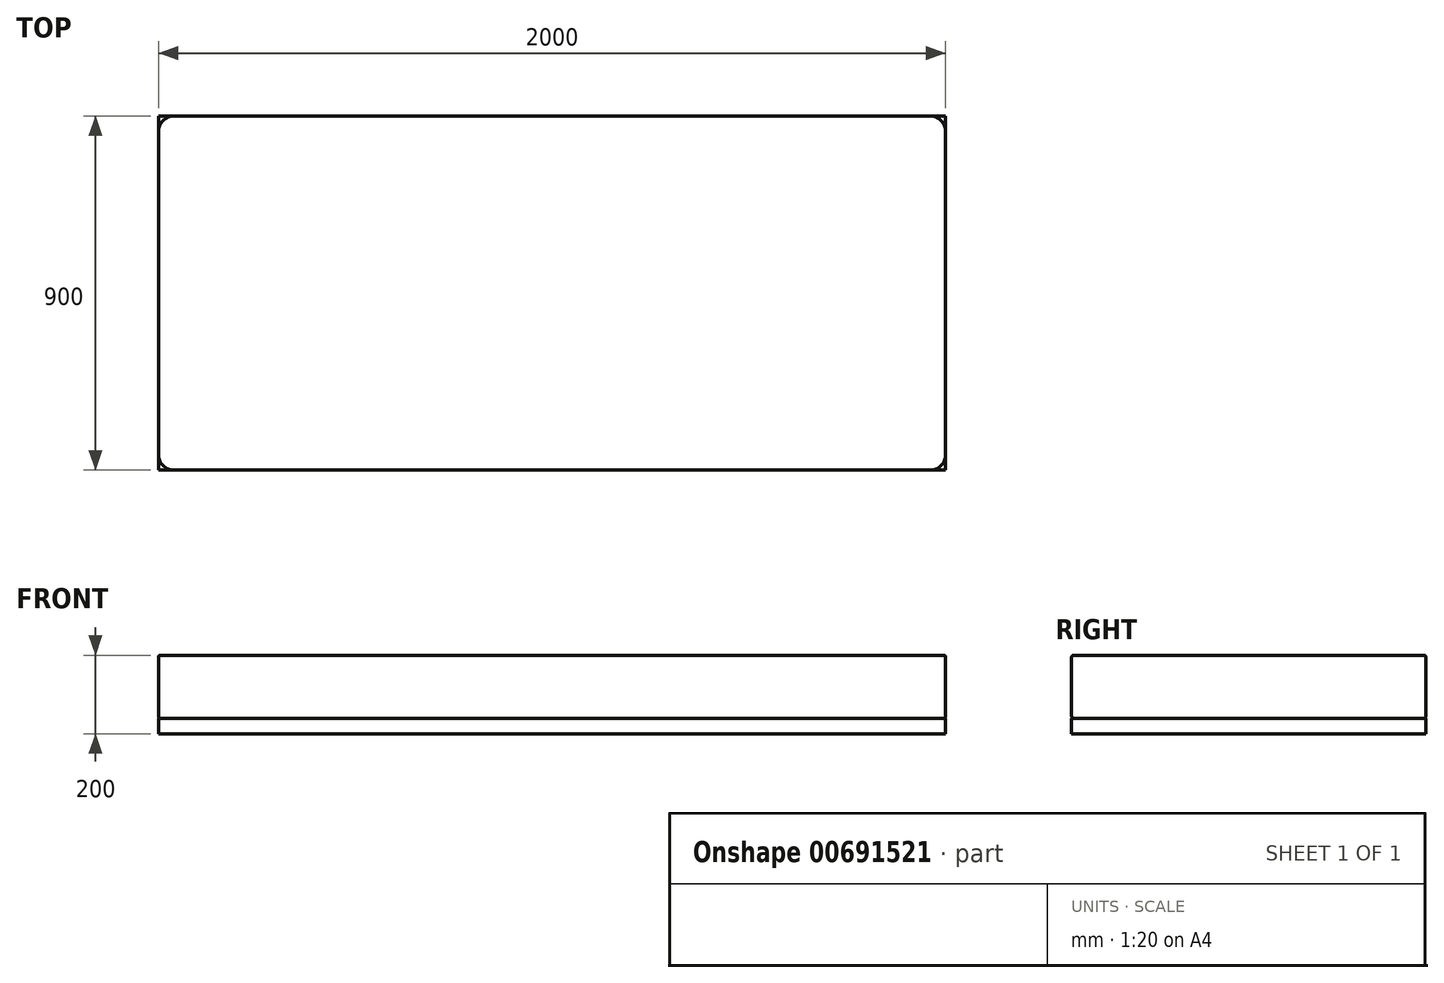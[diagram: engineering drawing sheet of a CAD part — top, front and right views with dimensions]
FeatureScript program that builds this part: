
annotation { "Feature Type Name" : "Feature", "Feature Type Description" : "" }
export const myFeature = defineFeature(function(context is Context, id is Id, definition is map)
    precondition{}
    {
        {
            var Q0;
            Q0=qCreatedBy(makeId("Top.planeOp"),FACE);
            var sketch = newSketch(context, id + "F0", { "sketchPlane" : qUnion([Q0])});
            skLineSegment(sketch, "E0.bottom", {"start": v(0, 0) * mm, "end": v(2000, 0) * mm});
            skLineSegment(sketch, "E0.top", {"start": v(0, -900) * mm, "end": v(2000, -900) * mm});
            skLineSegment(sketch, "E0.left", {"start": v(0, 0) * mm, "end": v(0, -900) * mm});
            skLineSegment(sketch, "E0.right", {"start": v(2000, 0) * mm, "end": v(2000, -900) * mm});
            skSolve(sketch);
        }
        {
            var Q0;
            Q0=makeQuery(id+"F0.imprint","IMPRINT",FACE,{"disambiguationData":[TD([[makeQuery(id+"F0.imprint","IMPRINT",EDGE,{"derivedFrom":sQuery(id+"F0.wireOp",EDGE,"E0.bottom")}),-1.0]])]});
            extrude(context, id + "F1", {"entities" : qUnion([Q0]), "depth" : 40 * mm, "offsetDistance" : 25 * mm});
        }
        {
            var Q0;
            Q0=makeQuery(id+"F1.opExtrude","CAP_FACE",FACE,{"disambiguationData":[OSD([sQuery(id+"F0.wireOp",EDGE,"E0.bottom"),sQuery(id+"F0.wireOp",EDGE,"E0.top"),sQuery(id+"F0.wireOp",EDGE,"E0.left"),sQuery(id+"F0.wireOp",EDGE,"E0.right")])],"isStart":false});
            extrude(context, id + "F2", {"entities" : qUnion([Q0]), "depth" : 160 * mm, "offsetDistance" : 25 * mm});
        }
        {
            var Q0;
            Q0=makeQuery(id+"F2.opExtrude","SWEPT_EDGE",EDGE,{"disambiguationData":[OSD([sQuery(id+"F0.wireOp",EDGE,"E0.top"),sQuery(id+"F0.wireOp",EDGE,"E0.left")])]});
            var Q1;
            Q1=makeQuery(id+"F2.opExtrude","SWEPT_EDGE",EDGE,{"disambiguationData":[OSD([sQuery(id+"F0.wireOp",EDGE,"E0.bottom"),sQuery(id+"F0.wireOp",EDGE,"E0.left")])]});
            var Q2;
            Q2=makeQuery(id+"F2.opExtrude","SWEPT_EDGE",EDGE,{"disambiguationData":[OSD([sQuery(id+"F0.wireOp",EDGE,"E0.top"),sQuery(id+"F0.wireOp",EDGE,"E0.right")])]});
            var Q3;
            Q3=makeQuery(id+"F2.opExtrude","SWEPT_EDGE",EDGE,{"disambiguationData":[OSD([sQuery(id+"F0.wireOp",EDGE,"E0.bottom"),sQuery(id+"F0.wireOp",EDGE,"E0.right")])]});
            fillet(context, id + "F3", {"entities" : qUnion([Q0, Q1, Q2, Q3]), "radius" : 40 * mm, "tangentPropagation" : true, "allowEdgeOverflow" : false});
        }
        {
            var Q0;
            Q0=makeQuery(id+"F2.opExtrude","CAP_EDGE",EDGE,{"disambiguationData":[OSD([sQuery(id+"F0.wireOp",EDGE,"E0.right")])],"isStart":false});
            var Q1;
            Q1=makeQuery(id+"F2.opExtrude","CAP_EDGE",EDGE,{"disambiguationData":[OSD([sQuery(id+"F0.wireOp",EDGE,"E0.left")])],"isStart":false});
            var Q2;
            Q2=makeQuery(id+"F2.opExtrude","CAP_EDGE",EDGE,{"disambiguationData":[OSD([sQuery(id+"F0.wireOp",EDGE,"E0.bottom")])],"isStart":true});
            var Q3;
            Q3=makeQuery(id+"F2.opExtrude","CAP_EDGE",EDGE,{"disambiguationData":[OSD([sQuery(id+"F0.wireOp",EDGE,"E0.bottom")])],"isStart":false});
            var Q4;
            Q4=makeQuery(id+"F2.opExtrude","CAP_EDGE",EDGE,{"disambiguationData":[OSD([sQuery(id+"F0.wireOp",EDGE,"E0.top")])],"isStart":false});
            var Q5;
            {var subQ0=sQuery(id+"F0.wireOp",EDGE,"E0.right");var subQ1=sQuery(id+"F0.wireOp",EDGE,"E0.bottom");Q5=makeQuery(id+"F3.opFillet","BLEND_EDGE",EDGE,{"blendedFrom":[makeQuery(id+"F2.opExtrude","SWEPT_EDGE",EDGE,{"disambiguationData":[OSD([subQ1,subQ0])]}),makeQuery(id+"F2.opExtrude","CAP_FACE",FACE,{"disambiguationData":[OSD([subQ1,sQuery(id+"F0.wireOp",EDGE,"E0.top"),sQuery(id+"F0.wireOp",EDGE,"E0.left"),subQ0])],"isStart":false})],"blendedInto":[makeQuery(id+"F2.opExtrude","CAP_FACE",FACE,{"disambiguationData":[OSD([subQ1,sQuery(id+"F0.wireOp",EDGE,"E0.top"),sQuery(id+"F0.wireOp",EDGE,"E0.left"),subQ0])],"isStart":false})]});}
            var Q6;
            {var subQ0=sQuery(id+"F0.wireOp",EDGE,"E0.top");Q6=makeQuery(id+"F3.opFillet","BLEND_EDGE",EDGE,{"blendedFrom":[makeQuery(id+"F2.opExtrude","SWEPT_EDGE",EDGE,{"disambiguationData":[OSD([subQ0,sQuery(id+"F0.wireOp",EDGE,"E0.left")])]}),makeQuery(id+"F2.opExtrude","SWEPT_FACE",FACE,{"disambiguationData":[OSD([subQ0])]})],"blendedInto":[makeQuery(id+"F2.opExtrude","SWEPT_FACE",FACE,{"disambiguationData":[OSD([subQ0])]})]});}
            var Q7;
            {var subQ0=sQuery(id+"F0.wireOp",EDGE,"E0.left");Q7=makeQuery(id+"F3.opFillet","BLEND_EDGE",EDGE,{"blendedFrom":[makeQuery(id+"F2.opExtrude","SWEPT_EDGE",EDGE,{"disambiguationData":[OSD([sQuery(id+"F0.wireOp",EDGE,"E0.top"),subQ0])]}),makeQuery(id+"F2.opExtrude","SWEPT_FACE",FACE,{"disambiguationData":[OSD([subQ0])]})],"blendedInto":[makeQuery(id+"F2.opExtrude","SWEPT_FACE",FACE,{"disambiguationData":[OSD([subQ0])]})]});}
            var Q8;
            Q8=makeQuery(id+"F2.opExtrude","CAP_EDGE",EDGE,{"disambiguationData":[OSD([sQuery(id+"F0.wireOp",EDGE,"E0.right")])],"isStart":true});
            var Q9;
            {var subQ0=sQuery(id+"F0.wireOp",EDGE,"E0.left");var subQ1=sQuery(id+"F0.wireOp",EDGE,"E0.bottom");Q9=makeQuery(id+"F3.opFillet","BLEND_EDGE",EDGE,{"blendedFrom":[makeQuery(id+"F2.opExtrude","SWEPT_EDGE",EDGE,{"disambiguationData":[OSD([subQ1,subQ0])]}),makeQuery(id+"F2.opExtrude","CAP_FACE",FACE,{"disambiguationData":[OSD([subQ1,sQuery(id+"F0.wireOp",EDGE,"E0.top"),subQ0,sQuery(id+"F0.wireOp",EDGE,"E0.right")])],"isStart":false})],"blendedInto":[makeQuery(id+"F2.opExtrude","CAP_FACE",FACE,{"disambiguationData":[OSD([subQ1,sQuery(id+"F0.wireOp",EDGE,"E0.top"),subQ0,sQuery(id+"F0.wireOp",EDGE,"E0.right")])],"isStart":false})]});}
            var Q10;
            Q10=makeQuery(id+"F2.opExtrude","CAP_EDGE",EDGE,{"disambiguationData":[OSD([sQuery(id+"F0.wireOp",EDGE,"E0.left")])],"isStart":true});
            var Q11;
            {var subQ0=sQuery(id+"F0.wireOp",EDGE,"E0.left");var subQ1=sQuery(id+"F0.wireOp",EDGE,"E0.top");Q11=makeQuery(id+"F3.opFillet","BLEND_EDGE",EDGE,{"blendedFrom":[makeQuery(id+"F2.opExtrude","SWEPT_EDGE",EDGE,{"disambiguationData":[OSD([subQ1,subQ0])]}),makeQuery(id+"F2.opExtrude","CAP_FACE",FACE,{"disambiguationData":[OSD([sQuery(id+"F0.wireOp",EDGE,"E0.bottom"),subQ1,subQ0,sQuery(id+"F0.wireOp",EDGE,"E0.right")])],"isStart":true})],"blendedInto":[makeQuery(id+"F2.opExtrude","CAP_FACE",FACE,{"disambiguationData":[OSD([sQuery(id+"F0.wireOp",EDGE,"E0.bottom"),subQ1,subQ0,sQuery(id+"F0.wireOp",EDGE,"E0.right")])],"isStart":true})]});}
            var Q12;
            {var subQ0=sQuery(id+"F0.wireOp",EDGE,"E0.bottom");Q12=makeQuery(id+"F3.opFillet","BLEND_EDGE",EDGE,{"blendedFrom":[makeQuery(id+"F2.opExtrude","SWEPT_EDGE",EDGE,{"disambiguationData":[OSD([subQ0,sQuery(id+"F0.wireOp",EDGE,"E0.left")])]}),makeQuery(id+"F2.opExtrude","SWEPT_FACE",FACE,{"disambiguationData":[OSD([subQ0])]})],"blendedInto":[makeQuery(id+"F2.opExtrude","SWEPT_FACE",FACE,{"disambiguationData":[OSD([subQ0])]})]});}
            var Q13;
            {var subQ0=sQuery(id+"F0.wireOp",EDGE,"E0.right");var subQ1=sQuery(id+"F0.wireOp",EDGE,"E0.bottom");Q13=makeQuery(id+"F3.opFillet","BLEND_EDGE",EDGE,{"blendedFrom":[makeQuery(id+"F2.opExtrude","SWEPT_EDGE",EDGE,{"disambiguationData":[OSD([subQ1,subQ0])]}),makeQuery(id+"F2.opExtrude","CAP_FACE",FACE,{"disambiguationData":[OSD([subQ1,sQuery(id+"F0.wireOp",EDGE,"E0.top"),sQuery(id+"F0.wireOp",EDGE,"E0.left"),subQ0])],"isStart":true})],"blendedInto":[makeQuery(id+"F2.opExtrude","CAP_FACE",FACE,{"disambiguationData":[OSD([subQ1,sQuery(id+"F0.wireOp",EDGE,"E0.top"),sQuery(id+"F0.wireOp",EDGE,"E0.left"),subQ0])],"isStart":true})]});}
            var Q14;
            {var subQ0=sQuery(id+"F0.wireOp",EDGE,"E0.left");Q14=makeQuery(id+"F3.opFillet","BLEND_EDGE",EDGE,{"blendedFrom":[makeQuery(id+"F2.opExtrude","SWEPT_EDGE",EDGE,{"disambiguationData":[OSD([sQuery(id+"F0.wireOp",EDGE,"E0.bottom"),subQ0])]}),makeQuery(id+"F2.opExtrude","SWEPT_FACE",FACE,{"disambiguationData":[OSD([subQ0])]})],"blendedInto":[makeQuery(id+"F2.opExtrude","SWEPT_FACE",FACE,{"disambiguationData":[OSD([subQ0])]})]});}
            var Q15;
            {var subQ0=sQuery(id+"F0.wireOp",EDGE,"E0.bottom");Q15=makeQuery(id+"F3.opFillet","BLEND_EDGE",EDGE,{"blendedFrom":[makeQuery(id+"F2.opExtrude","SWEPT_EDGE",EDGE,{"disambiguationData":[OSD([subQ0,sQuery(id+"F0.wireOp",EDGE,"E0.right")])]}),makeQuery(id+"F2.opExtrude","SWEPT_FACE",FACE,{"disambiguationData":[OSD([subQ0])]})],"blendedInto":[makeQuery(id+"F2.opExtrude","SWEPT_FACE",FACE,{"disambiguationData":[OSD([subQ0])]})]});}
            var Q16;
            {var subQ0=sQuery(id+"F0.wireOp",EDGE,"E0.right");Q16=makeQuery(id+"F3.opFillet","BLEND_EDGE",EDGE,{"blendedFrom":[makeQuery(id+"F2.opExtrude","SWEPT_EDGE",EDGE,{"disambiguationData":[OSD([sQuery(id+"F0.wireOp",EDGE,"E0.bottom"),subQ0])]}),makeQuery(id+"F2.opExtrude","SWEPT_FACE",FACE,{"disambiguationData":[OSD([subQ0])]})],"blendedInto":[makeQuery(id+"F2.opExtrude","SWEPT_FACE",FACE,{"disambiguationData":[OSD([subQ0])]})]});}
            var Q17;
            {var subQ0=sQuery(id+"F0.wireOp",EDGE,"E0.left");var subQ1=sQuery(id+"F0.wireOp",EDGE,"E0.top");Q17=makeQuery(id+"F3.opFillet","BLEND_EDGE",EDGE,{"blendedFrom":[makeQuery(id+"F2.opExtrude","SWEPT_EDGE",EDGE,{"disambiguationData":[OSD([subQ1,subQ0])]}),makeQuery(id+"F2.opExtrude","CAP_FACE",FACE,{"disambiguationData":[OSD([sQuery(id+"F0.wireOp",EDGE,"E0.bottom"),subQ1,subQ0,sQuery(id+"F0.wireOp",EDGE,"E0.right")])],"isStart":false})],"blendedInto":[makeQuery(id+"F2.opExtrude","CAP_FACE",FACE,{"disambiguationData":[OSD([sQuery(id+"F0.wireOp",EDGE,"E0.bottom"),subQ1,subQ0,sQuery(id+"F0.wireOp",EDGE,"E0.right")])],"isStart":false})]});}
            var Q18;
            Q18=makeQuery(id+"F2.opExtrude","CAP_EDGE",EDGE,{"disambiguationData":[OSD([sQuery(id+"F0.wireOp",EDGE,"E0.top")])],"isStart":true});
            var Q19;
            {var subQ0=sQuery(id+"F0.wireOp",EDGE,"E0.left");var subQ1=sQuery(id+"F0.wireOp",EDGE,"E0.bottom");Q19=makeQuery(id+"F3.opFillet","BLEND_EDGE",EDGE,{"blendedFrom":[makeQuery(id+"F2.opExtrude","SWEPT_EDGE",EDGE,{"disambiguationData":[OSD([subQ1,subQ0])]}),makeQuery(id+"F2.opExtrude","CAP_FACE",FACE,{"disambiguationData":[OSD([subQ1,sQuery(id+"F0.wireOp",EDGE,"E0.top"),subQ0,sQuery(id+"F0.wireOp",EDGE,"E0.right")])],"isStart":true})],"blendedInto":[makeQuery(id+"F2.opExtrude","CAP_FACE",FACE,{"disambiguationData":[OSD([subQ1,sQuery(id+"F0.wireOp",EDGE,"E0.top"),subQ0,sQuery(id+"F0.wireOp",EDGE,"E0.right")])],"isStart":true})]});}
            var Q20;
            {var subQ0=sQuery(id+"F0.wireOp",EDGE,"E0.right");Q20=makeQuery(id+"F3.opFillet","BLEND_EDGE",EDGE,{"blendedFrom":[makeQuery(id+"F2.opExtrude","SWEPT_EDGE",EDGE,{"disambiguationData":[OSD([sQuery(id+"F0.wireOp",EDGE,"E0.top"),subQ0])]}),makeQuery(id+"F2.opExtrude","SWEPT_FACE",FACE,{"disambiguationData":[OSD([subQ0])]})],"blendedInto":[makeQuery(id+"F2.opExtrude","SWEPT_FACE",FACE,{"disambiguationData":[OSD([subQ0])]})]});}
            var Q21;
            {var subQ0=sQuery(id+"F0.wireOp",EDGE,"E0.right");var subQ1=sQuery(id+"F0.wireOp",EDGE,"E0.top");Q21=makeQuery(id+"F3.opFillet","BLEND_EDGE",EDGE,{"blendedFrom":[makeQuery(id+"F2.opExtrude","SWEPT_EDGE",EDGE,{"disambiguationData":[OSD([subQ1,subQ0])]}),makeQuery(id+"F2.opExtrude","CAP_FACE",FACE,{"disambiguationData":[OSD([sQuery(id+"F0.wireOp",EDGE,"E0.bottom"),subQ1,sQuery(id+"F0.wireOp",EDGE,"E0.left"),subQ0])],"isStart":false})],"blendedInto":[makeQuery(id+"F2.opExtrude","CAP_FACE",FACE,{"disambiguationData":[OSD([sQuery(id+"F0.wireOp",EDGE,"E0.bottom"),subQ1,sQuery(id+"F0.wireOp",EDGE,"E0.left"),subQ0])],"isStart":false})]});}
            var Q22;
            {var subQ0=sQuery(id+"F0.wireOp",EDGE,"E0.right");var subQ1=sQuery(id+"F0.wireOp",EDGE,"E0.top");Q22=makeQuery(id+"F3.opFillet","BLEND_EDGE",EDGE,{"blendedFrom":[makeQuery(id+"F2.opExtrude","SWEPT_EDGE",EDGE,{"disambiguationData":[OSD([subQ1,subQ0])]}),makeQuery(id+"F2.opExtrude","CAP_FACE",FACE,{"disambiguationData":[OSD([sQuery(id+"F0.wireOp",EDGE,"E0.bottom"),subQ1,sQuery(id+"F0.wireOp",EDGE,"E0.left"),subQ0])],"isStart":true})],"blendedInto":[makeQuery(id+"F2.opExtrude","CAP_FACE",FACE,{"disambiguationData":[OSD([sQuery(id+"F0.wireOp",EDGE,"E0.bottom"),subQ1,sQuery(id+"F0.wireOp",EDGE,"E0.left"),subQ0])],"isStart":true})]});}
            var Q23;
            {var subQ0=sQuery(id+"F0.wireOp",EDGE,"E0.top");Q23=makeQuery(id+"F3.opFillet","BLEND_EDGE",EDGE,{"blendedFrom":[makeQuery(id+"F2.opExtrude","SWEPT_EDGE",EDGE,{"disambiguationData":[OSD([subQ0,sQuery(id+"F0.wireOp",EDGE,"E0.right")])]}),makeQuery(id+"F2.opExtrude","SWEPT_FACE",FACE,{"disambiguationData":[OSD([subQ0])]})],"blendedInto":[makeQuery(id+"F2.opExtrude","SWEPT_FACE",FACE,{"disambiguationData":[OSD([subQ0])]})]});}
            fillet(context, id + "F4", {"entities" : qUnion([Q0, Q1, Q2, Q3, Q4, Q5, Q6, Q7, Q8, Q9, Q10, Q11, Q12, Q13, Q14, Q15, Q16, Q17, Q18, Q19, Q20, Q21, Q22, Q23]), "radius" : 5 * mm, "tangentPropagation" : true, "allowEdgeOverflow" : false});
        }
    });
